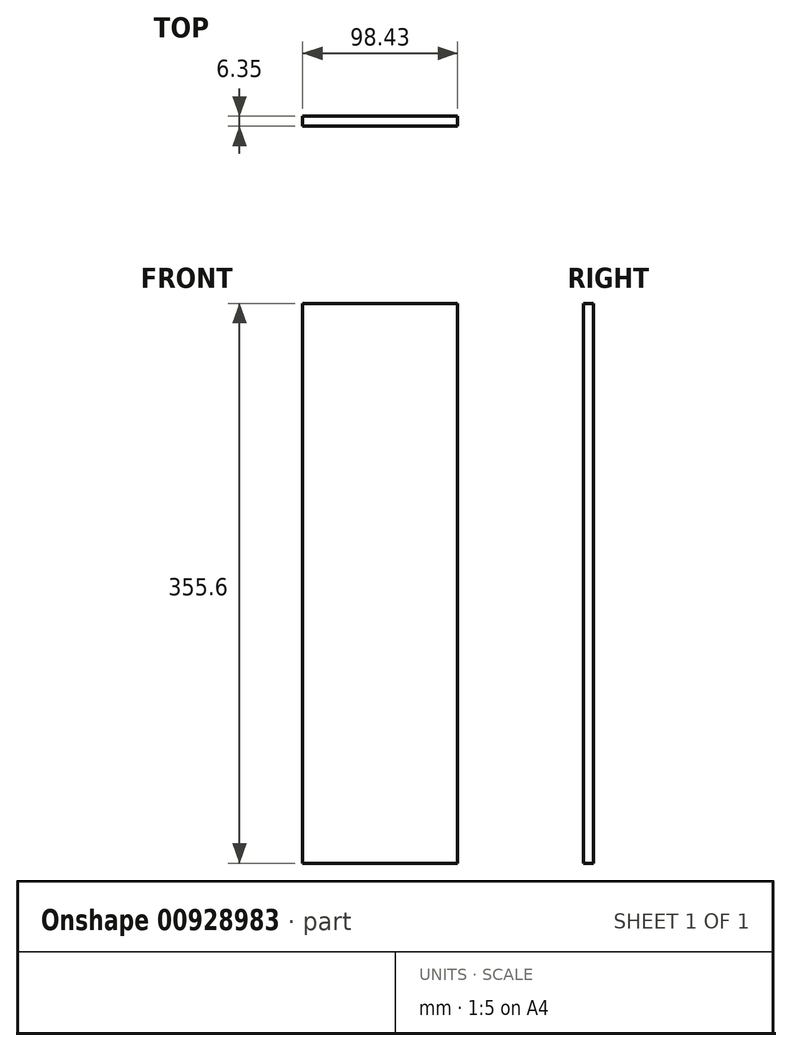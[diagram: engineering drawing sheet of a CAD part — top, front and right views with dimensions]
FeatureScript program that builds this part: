
annotation { "Feature Type Name" : "Feature", "Feature Type Description" : "" }
export const myFeature = defineFeature(function(context is Context, id is Id, definition is map)
    precondition{}
    {
        {
            var Q0;
            Q0=qCreatedBy(makeId("Front.planeOp"),FACE);
            var sketch = newSketch(context, id + "F0", { "sketchPlane" : qUnion([Q0])});
            skLineSegment(sketch, "E0.bottom", {"start": v(-84.08, 236.25) * mm, "end": v(14.35, 236.25) * mm});
            skLineSegment(sketch, "E0.top", {"start": v(-84.08, -119.35) * mm, "end": v(14.35, -119.35) * mm});
            skLineSegment(sketch, "E0.left", {"start": v(-84.08, 236.25) * mm, "end": v(-84.08, -119.35) * mm});
            skLineSegment(sketch, "E0.right", {"start": v(14.35, 236.25) * mm, "end": v(14.35, -119.35) * mm});
            skSolve(sketch);
        }
        {
            var Q0;
            Q0 = qSketchRegion(id + "F0", true);
            extrude(context, id + "F1", {"entities" : qUnion([Q0]), "flatOperationType" : FlatOperationType.REMOVE, "thickness" : 6.35 * mm, "thickness2" : 0 * mm, "thickness1" : 6.35 * mm, "depth" : 6.35 * mm, "offsetDistance" : 25.4 * mm, "startOffsetDistance" : 25.4 * mm, "startOffsetBound" : StartOffsetType.BLIND, "domain" : OperationDomain.MODEL});
        }
    });
